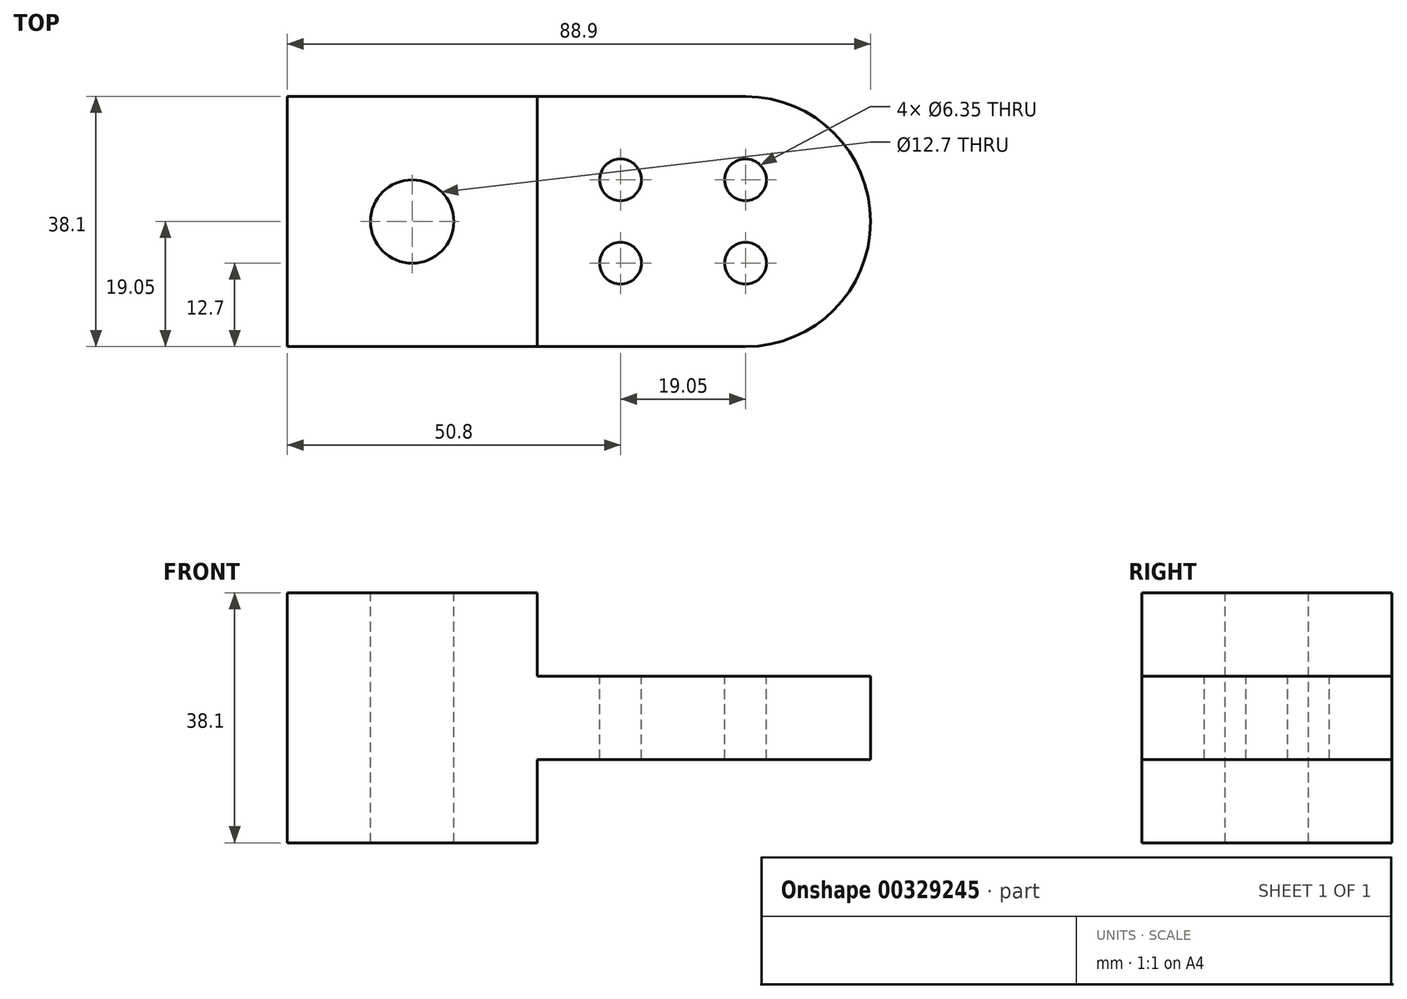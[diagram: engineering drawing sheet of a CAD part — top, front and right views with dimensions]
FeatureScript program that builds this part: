
annotation { "Feature Type Name" : "Feature", "Feature Type Description" : "" }
export const myFeature = defineFeature(function(context is Context, id is Id, definition is map)
    precondition{}
    {
        {
            var Q0;
            Q0=qCreatedBy(makeId("Top.planeOp"),FACE);
            var sketch = newSketch(context, id + "F0", { "sketchPlane" : qUnion([Q0])});
            skLineSegment(sketch, "E0.bottom", {"start": v(0, 0) * mm, "end": v(38.1, 0) * mm});
            skLineSegment(sketch, "E0.top", {"start": v(0, 38.1) * mm, "end": v(38.1, 38.1) * mm});
            skLineSegment(sketch, "E0.left", {"start": v(0, 0) * mm, "end": v(0, 38.1) * mm});
            skLineSegment(sketch, "E0.right", {"start": v(38.1, 0) * mm, "end": v(38.1, 38.1) * mm});
            skLineSegment(sketch, "E1", {"start": v(38.1, 38.1) * mm, "end": v(69.85, 38.1) * mm});
            skLineSegment(sketch, "E2", {"start": v(38.1, 0) * mm, "end": v(69.85, 0) * mm});
            skArc(sketch, "E3", {"start": v(69.85, 38.1) * mm, "mid": v(88.9, 19.05) * mm, "end": v(69.85, 0) * mm});
            skSolve(sketch);
        }
        {
            var Q0;
            Q0=makeQuery(id+"F0.imprint","IMPRINT",FACE,{"disambiguationData":[TD([[makeQuery(id+"F0.imprint","IMPRINT",EDGE,{"derivedFrom":sQuery(id+"F0.wireOp",EDGE,"E0.bottom")}),1.0]])]});
            extrude(context, id + "F1", {"entities" : qUnion([Q0]), "endBound" : BoundingType.SYMMETRIC, "depth" : 38.1 * mm});
        }
        {
            var Q0;
            Q0=makeQuery(id+"F0.imprint","IMPRINT",FACE,{"disambiguationData":[TD([[makeQuery(id+"F0.imprint","IMPRINT",EDGE,{"derivedFrom":sQuery(id+"F0.wireOp",EDGE,"E0.right")}),-1.0]])]});
            extrude(context, id + "F2", {"entities" : qUnion([Q0]), "operationType" : NewBodyOperationType.ADD, "endBound" : BoundingType.SYMMETRIC, "depth" : 12.7 * mm});
        }
        {
            var Q0;
            Q0=makeQuery(id+"F1.opExtrude","CAP_FACE",FACE,{"disambiguationData":[OSD([sQuery(id+"F0.wireOp",EDGE,"E0.bottom"),sQuery(id+"F0.wireOp",EDGE,"E0.top"),sQuery(id+"F0.wireOp",EDGE,"E0.left"),sQuery(id+"F0.wireOp",EDGE,"E0.right")])],"isStart":false});
            var sketch = newSketch(context, id + "F3", { "sketchPlane" : qUnion([Q0])});
            skCircle(sketch, "E4", {"center": v(19.05, 19.05) * mm, "radius": 6.35 * mm});
            skCircle(sketch, "E5", {"center": v(50.8, 25.4) * mm, "radius": 3.18 * mm});
            skCircle(sketch, "E6", {"center": v(69.85, 25.4) * mm, "radius": 3.18 * mm});
            skCircle(sketch, "E7", {"center": v(50.8, 12.7) * mm, "radius": 3.18 * mm});
            skCircle(sketch, "E8", {"center": v(69.85, 12.7) * mm, "radius": 3.18 * mm});
            skSolve(sketch);
        }
        {
            var Q0;
            Q0 = qSketchRegion(id + "F3", true);
            extrude(context, id + "F4", {"entities" : qUnion([Q0]), "operationType" : NewBodyOperationType.REMOVE, "endBound" : BoundingType.THROUGH_ALL, "oppositeDirection" : true, "depth" : 25.4 * mm});
        }
    });
